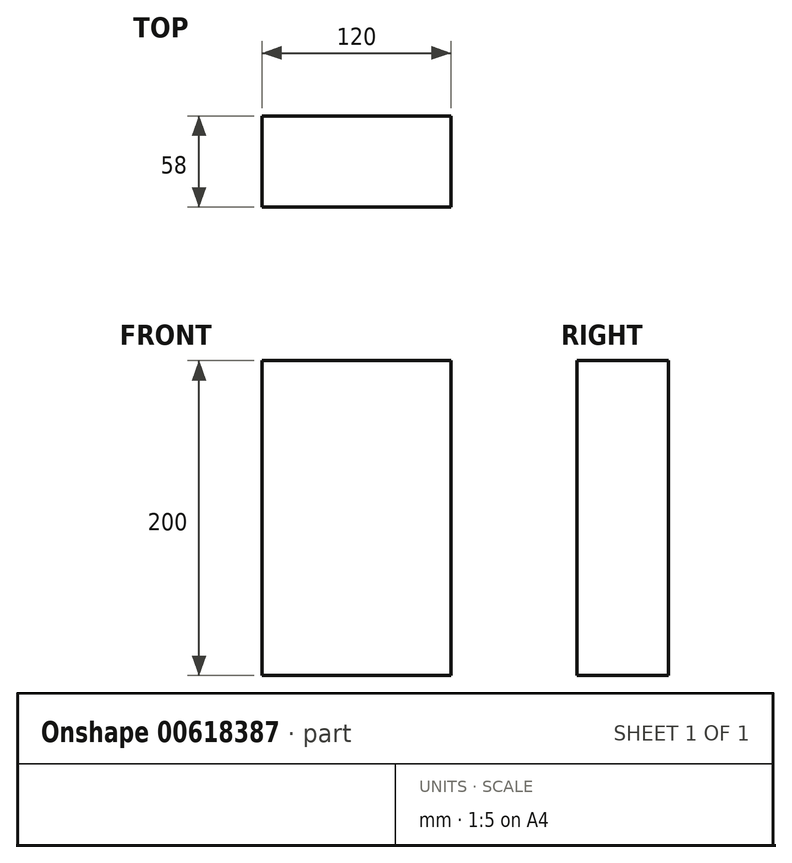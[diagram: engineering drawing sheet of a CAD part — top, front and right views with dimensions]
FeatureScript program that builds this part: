
annotation { "Feature Type Name" : "Feature", "Feature Type Description" : "" }
export const myFeature = defineFeature(function(context is Context, id is Id, definition is map)
    precondition{}
    {
        {
            var Q0;
            Q0=qCreatedBy(makeId("Top.planeOp"),FACE);
            var sketch = newSketch(context, id + "F0", { "sketchPlane" : qUnion([Q0])});
            skLineSegment(sketch, "E0.bottom", {"start": v(0, 0) * mm, "end": v(120, 0) * mm});
            skLineSegment(sketch, "E0.top", {"start": v(0, 58) * mm, "end": v(120, 58) * mm});
            skLineSegment(sketch, "E0.left", {"start": v(0, 0) * mm, "end": v(0, 58) * mm});
            skLineSegment(sketch, "E0.right", {"start": v(120, 0) * mm, "end": v(120, 58) * mm});
            skSolve(sketch);
        }
        {
            var Q0;
            Q0=makeQuery(id+"F0.imprint","IMPRINT",FACE,{"disambiguationData":[TD([[makeQuery(id+"F0.imprint","IMPRINT",EDGE,{"derivedFrom":sQuery(id+"F0.wireOp",EDGE,"E0.bottom")}),1.0]])]});
            extrude(context, id + "F1", {"entities" : qUnion([Q0]), "depth" : 200 * mm, "offsetDistance" : 25 * mm});
        }
    });
